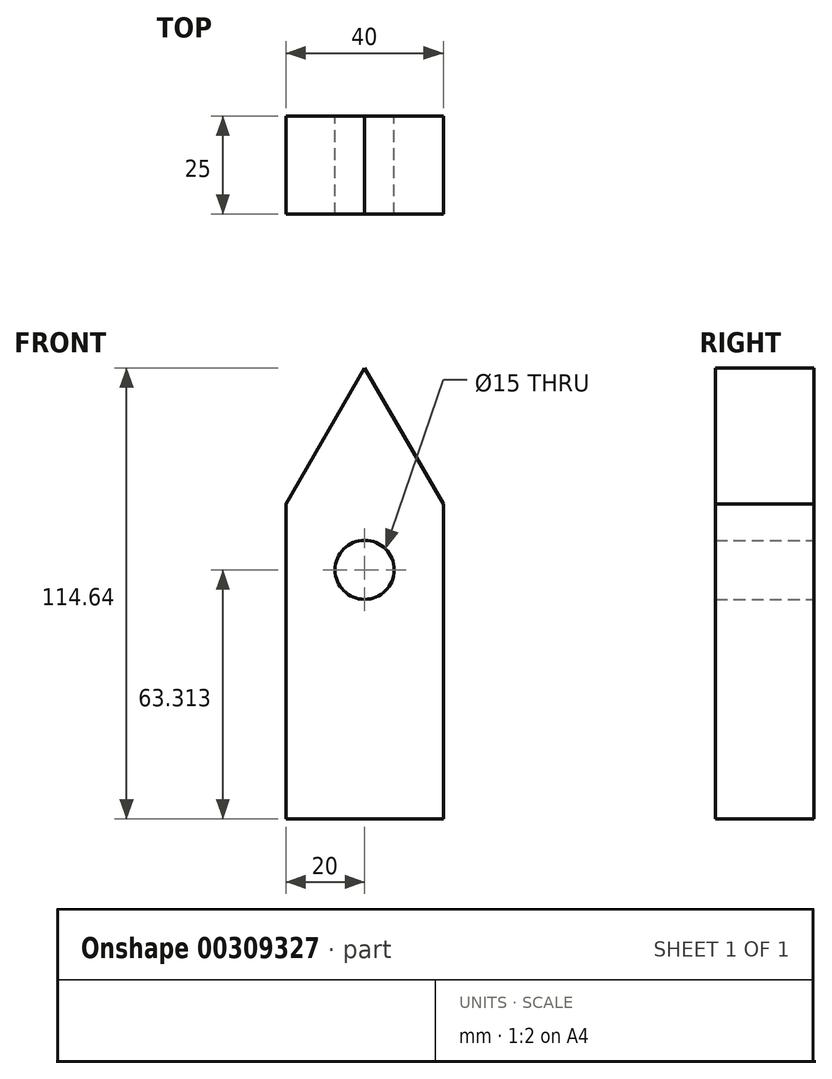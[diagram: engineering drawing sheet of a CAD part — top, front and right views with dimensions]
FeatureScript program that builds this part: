
annotation { "Feature Type Name" : "Feature", "Feature Type Description" : "" }
export const myFeature = defineFeature(function(context is Context, id is Id, definition is map)
    precondition{}
    {
        {
            var Q0;
            Q0=qCreatedBy(makeId("Front.planeOp"),FACE);
            var sketch = newSketch(context, id + "F0", { "sketchPlane" : qUnion([Q0])});
            skLineSegment(sketch, "E0.bottom", {"start": v(20, 40) * mm, "end": v(-20, 40) * mm});
            skLineSegment(sketch, "E0.top", {"start": v(20, -40) * mm, "end": v(-20, -40) * mm});
            skLineSegment(sketch, "E0.left", {"start": v(20, 40) * mm, "end": v(20, -40) * mm});
            skLineSegment(sketch, "E0.right", {"start": v(-20, 40) * mm, "end": v(-20, -40) * mm});
            skPoint(sketch, "E0.middle", {"position": v(0, 0) * mm});
            skCircle(sketch, "E1", {"center": v(0, 23.31) * mm, "radius": 7.5 * mm});
            skLineSegment(sketch, "E2", {"start": v(-20, 40) * mm, "end": v(0, 74.64) * mm});
            skLineSegment(sketch, "E3", {"start": v(0, 74.64) * mm, "end": v(20, 40) * mm});
            skSolve(sketch);
        }
        {
            var Q0;
            Q0 = qSketchRegion(id + "F0", true);
            extrude(context, id + "F1", {"entities" : qUnion([Q0]), "depth" : 25 * mm});
        }
    });
